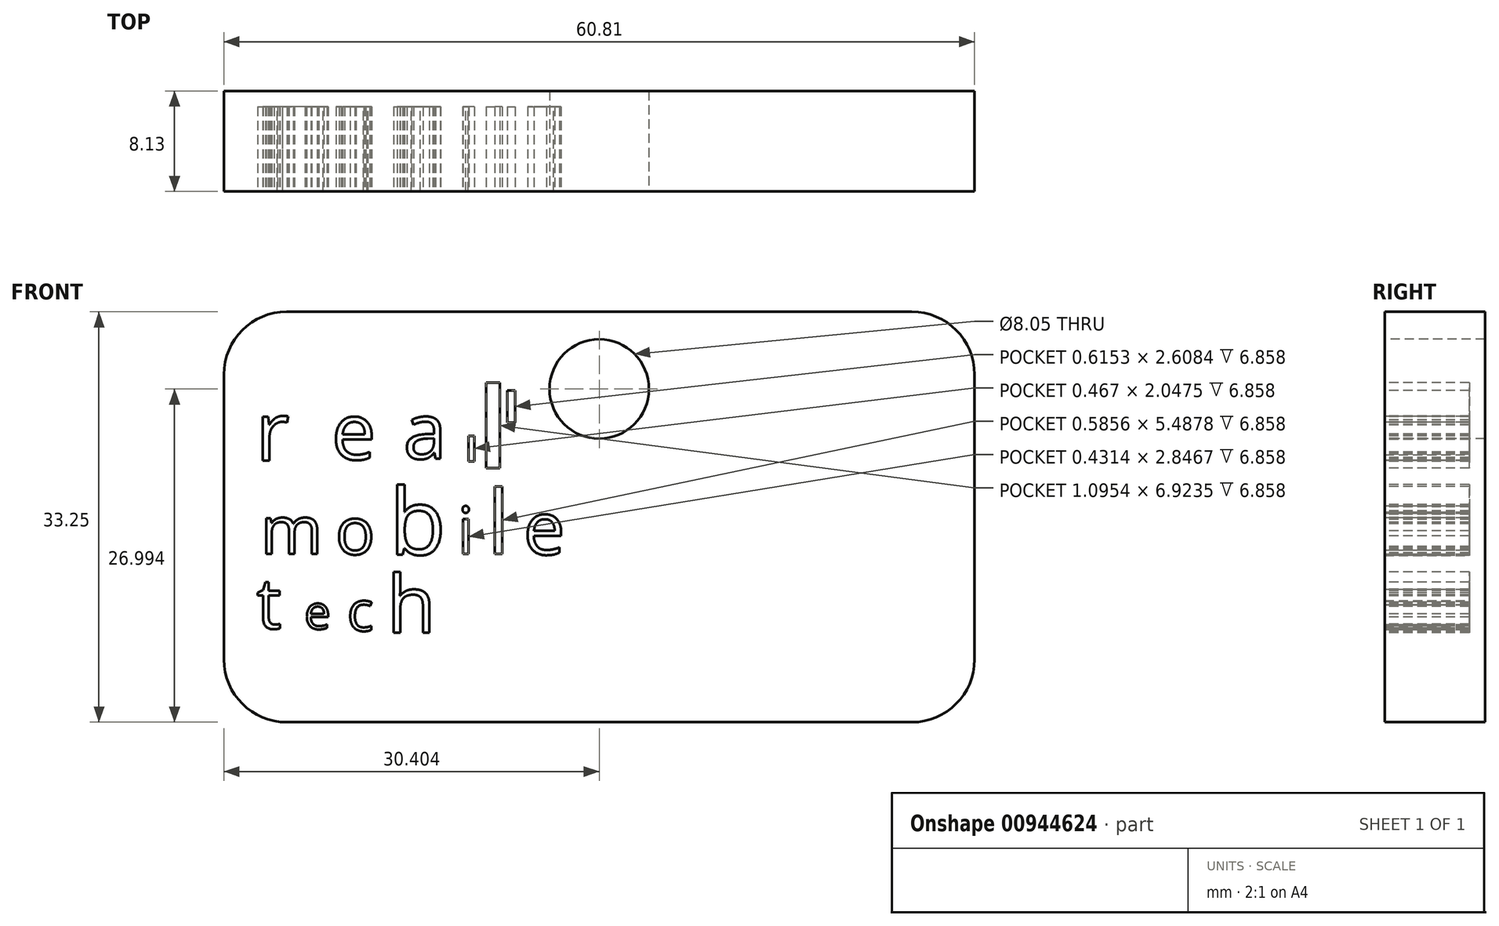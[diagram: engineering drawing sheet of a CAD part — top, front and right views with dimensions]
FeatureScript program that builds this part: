
annotation { "Feature Type Name" : "Feature", "Feature Type Description" : "" }
export const myFeature = defineFeature(function(context is Context, id is Id, definition is map)
    precondition{}
    {
        {
            var Q0;
            Q0=qCreatedBy(makeId("Front.planeOp"),FACE);
            var sketch = newSketch(context, id + "F0", { "sketchPlane" : qUnion([Q0])});
            skLineSegment(sketch, "E0", {"start": v(0, 0) * mm, "end": v(-46.08, 0) * mm});
            skLineSegment(sketch, "E1", {"start": v(0, 0) * mm, "end": v(14.73, 0) * mm});
            skLineSegment(sketch, "E2", {"start": v(-46.08, 0) * mm, "end": v(-46.08, 32.44) * mm});
            skLineSegment(sketch, "E3", {"start": v(14.73, 0) * mm, "end": v(14.73, 33.25) * mm});
            skCircle(sketch, "E4", {"center": v(-15.68, 27) * mm, "radius": 4.03 * mm});
            skPoint(sketch, "E4.centerSnap0", {"position": v(-15.68, 32.85) * mm});
            skLineSegment(sketch, "E5", {"start": v(14.73, 33.25) * mm, "end": v(-46.2, 33.25) * mm});
            skLineSegment(sketch, "E6", {"start": v(-46.2, 33.25) * mm, "end": v(-46.08, 32.05) * mm});
            skSolve(sketch);
        }
        {
            var Q0;
            {var subQ1=sQuery(id+"F0.wireOp",EDGE,"E0");Q0=makeQuery(id+"F0.imprint","IMPRINT",FACE,{"disambiguationData":[TD([[makeQuery(id+"F0.imprint","IMPRINT",EDGE,{"derivedFrom":subQ1}),-1.0]])]});}
            extrude(context, id + "F1", {"entities" : qUnion([Q0]), "oppositeDirection" : true, "depth" : 8.13 * mm, "offsetDistance" : 25.4 * mm});
        }
        {
            var Q0;
            Q0=makeQuery(id+"F1.opExtrude","CAP_FACE",FACE,{"disambiguationData":[OSD([sQuery(id+"F0.wireOp",EDGE,"E0"),sQuery(id+"F0.wireOp",EDGE,"E1"),sQuery(id+"F0.wireOp",EDGE,"E2"),sQuery(id+"F0.wireOp",EDGE,"E3"),sQuery(id+"F0.wireOp",EDGE,"E4"),sQuery(id+"F0.wireOp",EDGE,"E5"),sQuery(id+"F0.wireOp",EDGE,"E6")])],"isStart":true});
            var sketch = newSketch(context, id + "F2", { "sketchPlane" : qUnion([Q0])});
            skText(sketch, "E7", { "text": "r", "fontName": "OpenSans-Regular.ttf"});
            skText(sketch, "E8", { "text": "e", "fontName": "OpenSans-Regular.ttf"});
            skText(sketch, "E9", { "text": "a\n", "fontName": "OpenSans-Regular.ttf"});
            skText(sketch, "E10", { "text": "m\n", "fontName": "OpenSans-Regular.ttf"});
            skText(sketch, "E11", { "text": "o", "fontName": "OpenSans-Regular.ttf"});
            skText(sketch, "E12", { "text": "b\n", "fontName": "OpenSans-Regular.ttf"});
            skText(sketch, "E13", { "text": "i", "fontName": "OpenSans-Regular.ttf"});
            skText(sketch, "E14", { "text": "l", "fontName": "OpenSans-Regular.ttf"});
            skText(sketch, "E15", { "text": "e", "fontName": "OpenSans-Regular.ttf"});
            skText(sketch, "E16", { "text": "t", "fontName": "OpenSans-Regular.ttf"});
            skText(sketch, "E17", { "text": "e", "fontName": "OpenSans-Regular.ttf"});
            skText(sketch, "E18", { "text": "c", "fontName": "OpenSans-Regular.ttf"});
            skText(sketch, "E19", { "text": "h", "fontName": "OpenSans-Regular.ttf"});
            skLineSegment(sketch, "E20", {"start": v(-24.83, 27.52) * mm, "end": v(-24.83, 21.53) * mm});
            skLineSegment(sketch, "E21", {"start": v(-24.83, 21.53) * mm, "end": v(-24.83, 20.6) * mm});
            skLineSegment(sketch, "E22", {"start": v(-24.83, 20.6) * mm, "end": v(-23.73, 20.6) * mm});
            skLineSegment(sketch, "E23", {"start": v(-26.26, 23.18) * mm, "end": v(-26.26, 21.14) * mm});
            skLineSegment(sketch, "E24", {"start": v(-26.26, 21.14) * mm, "end": v(-25.8, 21.14) * mm});
            skLineSegment(sketch, "E25", {"start": v(-25.8, 21.14) * mm, "end": v(-25.8, 23.18) * mm});
            skLineSegment(sketch, "E26", {"start": v(-25.8, 23.18) * mm, "end": v(-26.26, 23.18) * mm});
            skLineSegment(sketch, "E27", {"start": v(-23.73, 20.6) * mm, "end": v(-23.73, 27.52) * mm});
            skLineSegment(sketch, "E28", {"start": v(-24.83, 27.52) * mm, "end": v(-23.73, 27.52) * mm});
            skLineSegment(sketch, "E29", {"start": v(-23.11, 24.27) * mm, "end": v(-22.5, 24.27) * mm});
            skLineSegment(sketch, "E30", {"start": v(-22.5, 24.27) * mm, "end": v(-22.5, 26.86) * mm});
            skLineSegment(sketch, "E31", {"start": v(-23.11, 24.27) * mm, "end": v(-23.11, 26.88) * mm});
            skLineSegment(sketch, "E32", {"start": v(-23.11, 26.88) * mm, "end": v(-22.5, 26.86) * mm});
            const initialGuessF2  = {"E7": [-0.0435, 0.0212, 1, 0, 0.00478], "E8": [-0.03737, 0.02127, 1, 0, 0.00461], "E9": [-0.03155, 0.02134, 1, 0, 0.00454], "E10": [-0.04313, 0.01362, 1, 0, 0.00391], "E11": [-0.03706, 0.0136, 1, 0, 0.00383], "E12": [-0.03268, 0.01357, 1, 0, 0.00537], "E13": [-0.02717, 0.01362, 1, 0, 0.00383], "E14": [-0.02475, 0.01362, 1, 0, 0.0052], "E15": [-0.02182, 0.01358, 1, 0, 0.00432], "E16": [-0.04344, 0.00758, 1, 0, 0.00412], "E17": [-0.03958, 0.00755, 1, 0, 0.00274], "E18": [-0.0361, 0.0074, 1, 0, 0.00323], "E19": [-0.03288, 0.00726, 1, 0, 0.00464]};
            skSetInitialGuess(sketch, initialGuessF2);
            skSolve(sketch);
        }
        {
            var Q0;
            Q0 = qSketchRegion(id + "F2", true);
            extrude(context, id + "F3", {"entities" : qUnion([Q0]), "operationType" : NewBodyOperationType.REMOVE, "oppositeDirection" : true, "depth" : 6.86 * mm, "offsetDistance" : 25.4 * mm});
        }
        {
            var Q0;
            Q0=makeQuery(id+"F1.opExtrude","SWEPT_EDGE",EDGE,{"disambiguationData":[OSD([sQuery(id+"F0.wireOp",EDGE,"E3"),sQuery(id+"F0.wireOp",EDGE,"E5")])]});
            var Q1;
            Q1=makeQuery(id+"F1.opExtrude","SWEPT_EDGE",EDGE,{"disambiguationData":[OSD([sQuery(id+"F0.wireOp",EDGE,"E5"),sQuery(id+"F0.wireOp",EDGE,"E6")])]});
            var Q2;
            Q2=makeQuery(id+"F1.opExtrude","SWEPT_EDGE",EDGE,{"disambiguationData":[OSD([sQuery(id+"F0.wireOp",EDGE,"E0"),sQuery(id+"F0.wireOp",EDGE,"E2")])]});
            var Q3;
            Q3=makeQuery(id+"F1.opExtrude","SWEPT_EDGE",EDGE,{"disambiguationData":[OSD([sQuery(id+"F0.wireOp",EDGE,"E1"),sQuery(id+"F0.wireOp",EDGE,"E3")])]});
            fillet(context, id + "F4", {"entities" : qUnion([Q0, Q1, Q2, Q3]), "radius" : 5.08 * mm, "tangentPropagation" : true, "allowEdgeOverflow" : false});
        }
        {
            var Q0;
            Q0=makeQuery(id+"F4.opFillet","BLEND_EDGE",EDGE,{"blendedFrom":[makeQuery(id+"F1.opExtrude","SWEPT_EDGE",EDGE,{"disambiguationData":[OSD([sQuery(id+"F0.wireOp",EDGE,"E5"),sQuery(id+"F0.wireOp",EDGE,"E6")])]}),makeQuery(id+"F1.opExtrude","SWEPT_FACE",FACE,{"disambiguationData":[OSD([sQuery(id+"F0.wireOp",EDGE,"E2")])]})],"blendedInto":[makeQuery(id+"F1.opExtrude","SWEPT_FACE",FACE,{"disambiguationData":[OSD([sQuery(id+"F0.wireOp",EDGE,"E2")])]})]});
            fillet(context, id + "F5", {"entities" : qUnion([Q0]), "radius" : 5.08 * mm, "tangentPropagation" : true, "allowEdgeOverflow" : false});
        }
    });
